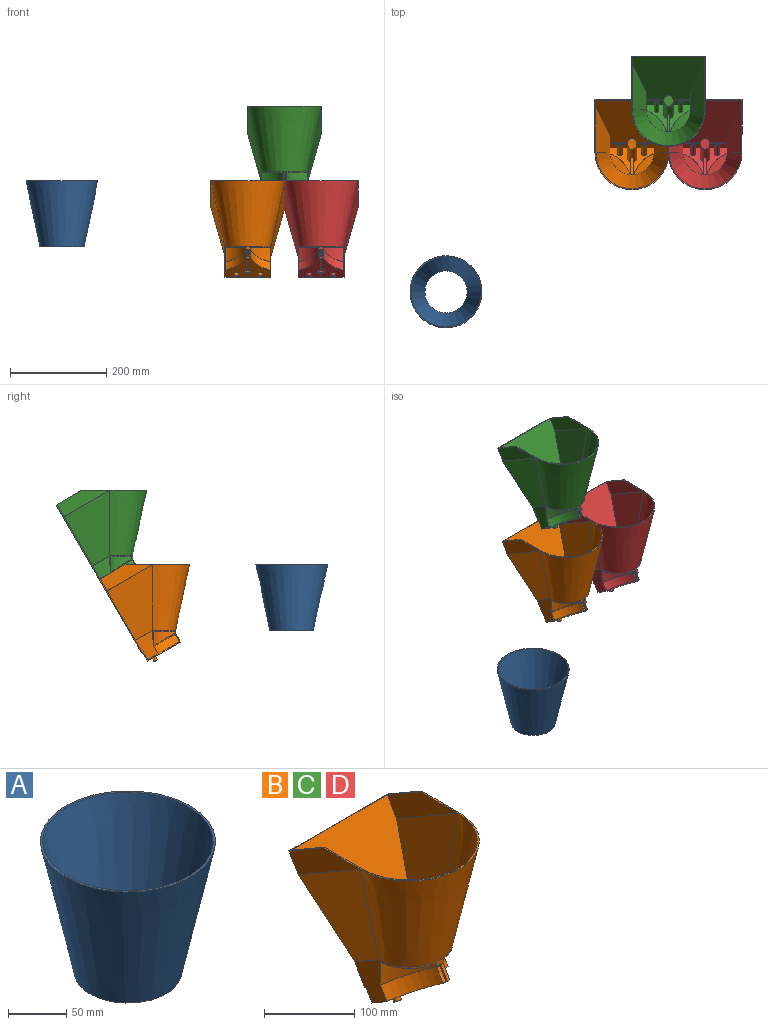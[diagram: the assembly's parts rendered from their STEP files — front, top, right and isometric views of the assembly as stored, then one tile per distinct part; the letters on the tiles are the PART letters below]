
ASSEMBLY  parts=4 mates=5
PART A: 4 faces, bbox 150x150x137 mm
  f0: cone r=73mm half-angle=12deg, axis (0,0,1), area 51428.7mm2, adj f1,f3
  f1: plane 150x150mm, normal (0,0,1), area 929.9mm2, adj f0,f2
  f2: cone r=75mm half-angle=12deg, axis (0,0,1), area 53188.7mm2, adj f1,f3
  f3: plane 91.76x91.76mm, normal (0,0,-1), area 564mm2, adj f0,f2
PART B: 80 faces, bbox 156.9x191.3x205.4 mm
  f0: plane 24.56x23.54mm, normal (-1,0,0), area 307.9mm2, adj f3,f14,f22,f74
  f1: plane 50.5x40.99mm, normal (1,0,0), area 899.7mm2, adj f2,f4,f9,f53,f74
  f2: plane 40.52x23.4mm, normal (0,-0.5,-0.87), area 93.5mm2, adj f1,f9,f10,f74
  f3: plane 68.78x46.88mm, normal (0,-0.5,-0.87), area 2119.8mm2, adj f0,f10,f14,f16,f51,f52,f74,f78
  f4: plane 68.78x46.88mm, normal (0,-0.5,-0.87), area 2119.8mm2, adj f1,f12,f17,f48,f53,f54,f74,f76
  f5: plane 37.52x21.66mm, normal (0,0.5,0.87), area 258.1mm2, adj f7,f13,f50,f66
  f6: plane 25.96x22.87mm, normal (0,0,1), area 362.8mm2, adj f50
  f7: plane 47.02x38.12mm, normal (-1,0,0), area 823.2mm2, adj f5,f50,f59,f60
  f8: cylinder r=47.88mm len=10.15mm, axis (0,0,1), area 69.5mm2, adj f9,f18,f19,f33,f45,f47,f52,f53
  f9: extruded ~2.31x2mm, area 4.6mm2, adj f1,f2,f8,f10
  f10: plane 50.5x40.99mm, normal (-1,0,0), area 899.7mm2, adj f2,f3,f9,f52,f74
  f11: plane 152.98x150mm, normal (0,-0.87,0.5), area 21352.9mm2, adj f27,f28,f29,f30,f34,f36,f49,f55
  f12: plane 24.56x23.54mm, normal (1,0,0), area 307.9mm2, adj f4,f22,f48,f74
  f13: plane 47.02x38.12mm, normal (1,0,0), area 823.2mm2, adj f5,f50,f61,f65
  f14: plane 46.88x16.45mm, normal (0,0.87,-0.5), area 890.7mm2, adj f0,f3,f16,f22
  f15: plane 154.71x154mm, normal (0,0.87,-0.5), area 22251mm2, adj f16,f17,f22,f25,f26,f35,f37,f49
  f16: plane 64.03x50.11mm, normal (1,0,0), area 1619.1mm2, adj f3,f14,f15,f19,f20,f22,f37,f39
  f17: plane 64.03x50.11mm, normal (-1,0,0), area 1619.1mm2, adj f4,f15,f18,f22,f23,f35,f38,f48
  f18: cylinder r=75mm len=45.14mm, axis (0,0,1), area 1279.3mm2, adj f8,f17,f23,f38,f46,f54
  f19: cylinder r=75mm len=45.14mm, axis (0,0,1), area 1279.3mm2, adj f8,f16,f20,f39,f44,f51
  f20: cylinder r=47.88mm len=21.65mm, axis (0,0,1), area 48.7mm2, adj f16,f19,f33,f39,f45
  f21: cylinder r=45.88mm len=5.93mm, axis (0,0,1), area 3.7mm2, adj f31,f42,f61,f67
  f22: plane 95.76x15.77mm, normal (0,-0.5,-0.87), area 223.8mm2, adj f0,f12,f14,f15,f16,f17,f48,f74
  f23: cylinder r=47.88mm len=21.65mm, axis (0,0,1), area 48.7mm2, adj f17,f18,f33,f38,f47
  f24: cylinder r=45.88mm len=5.93mm, axis (0,0,1), area 3.7mm2, adj f31,f40,f59,f67
  f25: plane 111.46x55.98mm, normal (-1,0,0), area 2518.7mm2, adj f15,f32,f35,f49
  f26: plane 111.46x55.98mm, normal (1,0,0), area 2518.7mm2, adj f15,f32,f37,f49
  f27: plane 61.4x47.08mm, normal (-1,0,0), area 1465.3mm2, adj f11,f31,f36,f42,f55,f62,f63,f65
  f28: plane 61.4x47.08mm, normal (1,0,0), area 1465.3mm2, adj f11,f31,f34,f40,f55,f57,f58,f60
  f29: plane 109.73x54.98mm, normal (1,0,0), area 2460.7mm2, adj f11,f32,f34,f49
  f30: plane 109.73x54.98mm, normal (-1,0,0), area 2460.7mm2, adj f11,f32,f36,f49
  f31: cone r=75mm half-angle=12deg, axis (0,0,1), area 26596.2mm2, adj f21,f24,f27,f28,f32,f34,f36,f40
  f32: plane 154x135mm, normal (0,0,1), area 709.5mm2, adj f25,f26,f29,f30,f31,f33,f49
  f33: cone r=77mm half-angle=12deg, axis (0,0,1), area 27474.4mm2, adj f8,f20,f23,f32,f35,f37,f45,f47
  f34: plane 157.73x95.23mm, normal (0.97,0.12,0.21), area 9249.9mm2, adj f11,f28,f29,f31
  f35: plane 158.73x96.96mm, normal (-0.97,-0.12,-0.21), area 9494.2mm2, adj f15,f17,f25,f33
  f36: plane 157.73x95.23mm, normal (-0.97,0.12,0.21), area 9249.9mm2, adj f11,f27,f30,f31
  f37: plane 158.73x96.96mm, normal (0.97,-0.12,-0.21), area 9494.2mm2, adj f15,f16,f26,f33
  f38: bspline ~9.2x4.98mm, area 2.9mm2, adj f17,f18,f23
  f39: bspline ~9.2x4.98mm, area 2.9mm2, adj f16,f19,f20
  f40: cylinder r=77mm len=44.6mm, axis (0,0,1), area 1295mm2, adj f24,f28,f31,f41,f58
  f41: plane 44.6x42.25mm, normal (0,0,1), area 761.2mm2, adj f31,f40
  f42: cylinder r=77mm len=44.6mm, axis (0,0,1), area 1295mm2, adj f21,f27,f31,f43,f62
  f43: plane 44.6x42.25mm, normal (0,0,1), area 761.2mm2, adj f31,f42
  f44: plane 45.13x42.75mm, normal (0,0,-1), area 768.8mm2, adj f19,f45
  f45: extruded ~45.11x42.74mm, area 135.3mm2, adj f8,f20,f33,f44
  f46: plane 45.13x42.75mm, normal (0,0,-1), area 768.8mm2, adj f18,f47
  f47: extruded ~45.11x42.74mm, area 135.2mm2, adj f8,f23,f33,f46
  f48: plane 46.88x16.45mm, normal (0,0.87,-0.5), area 890.7mm2, adj f4,f12,f17,f22
  f49: plane 154x53.46mm, normal (0,0.5,0.87), area 546.9mm2, adj f11,f15,f25,f26,f29,f30,f32
  f50: cylinder r=10mm len=64.67mm, axis (0,-0.5,-0.87), area 3384.3mm2, adj f5,f6,f7,f13,f55,f56,f60,f64
  f51: extruded ~55.14x43.38mm, area 1389.5mm2, adj f3,f16,f19,f52
  f52: extruded ~17.47x10.26mm, area 81.8mm2, adj f3,f8,f10,f51
  f53: extruded ~17.47x10.26mm, area 81.8mm2, adj f1,f4,f8,f54
  f54: extruded ~55.14x43.38mm, area 1389.5mm2, adj f4,f17,f18,f53
  f55: plane 91.76x13.65mm, normal (0,0.5,0.87), area 264.2mm2, adj f11,f27,f28,f50,f56,f57,f63,f64
  f56: plane 23.33x21.42mm, normal (-1,0,0), area 261.4mm2, adj f50,f55,f57,f60
  f57: plane 42.88x16.45mm, normal (0,-0.87,0.5), area 814.7mm2, adj f28,f55,f56,f60
  f58: extruded ~54.6x43.07mm, area 1369.3mm2, adj f28,f40,f59,f60
  f59: extruded ~17.35x10.04mm, area 12.4mm2, adj f7,f24,f58,f60,f66
  f60: plane 65.96x42.88mm, normal (0,0.5,0.87), area 1708.7mm2, adj f7,f28,f50,f56,f57,f58,f59,f69
  f61: extruded ~17.35x10.04mm, area 12.4mm2, adj f13,f21,f62,f65,f66
  f62: extruded ~54.6x43.07mm, area 1369.3mm2, adj f27,f42,f61,f65
  f63: plane 42.88x16.45mm, normal (0,-0.87,0.5), area 814.7mm2, adj f27,f55,f64,f65
  f64: plane 23.33x21.42mm, normal (1,0,0), area 261.4mm2, adj f50,f55,f63,f65
  f65: plane 65.96x42.88mm, normal (0,0.5,0.87), area 1708.7mm2, adj f13,f27,f50,f61,f62,f63,f64,f73
  f66: plane 6x0.87mm, normal (0,0.87,-0.5), area 6mm2, adj f5,f59,f61,f67
  f67: plane 6.02x5.91mm, normal (0,1,0), area 33.6mm2, adj f21,f24,f31,f66
  f68: cylinder r=2.5mm len=45.8mm, axis (0,-0.5,-0.87), area 785.4mm2, adj f70,f77
  f69: cylinder r=4.5mm len=39.14mm, axis (0,-0.5,-0.87), area 1131mm2, adj f60,f70
  f70: plane 9x7.79mm, normal (0,0.5,0.87), area 44mm2, adj f68,f69
  f71: plane 9x7.79mm, normal (0,0.5,0.87), area 44mm2, adj f72,f73
  f72: cylinder r=2.5mm len=45.8mm, axis (0,-0.5,-0.87), area 785.4mm2, adj f71,f79
  f73: cylinder r=4.5mm len=39.14mm, axis (0,-0.5,-0.87), area 1131mm2, adj f65,f71
  f74: cylinder r=8mm len=61.98mm, axis (0,-0.5,-0.87), area 2823.6mm2, adj f0,f1,f2,f3,f4,f10,f12,f22
  f75: plane 18.48x16mm, normal (0,0,-1), area 232.2mm2, adj f74
  f76: cylinder r=4.5mm len=11.79mm, axis (0,0.5,0.87), area 226.2mm2, adj f4,f77
  f77: plane 9x7.79mm, normal (0,-0.5,-0.87), area 44mm2, adj f68,f76
  f78: cylinder r=4.5mm len=11.79mm, axis (0,0.5,0.87), area 226.2mm2, adj f3,f79
  f79: plane 9x7.79mm, normal (0,-0.5,-0.87), area 44mm2, adj f72,f78
PART C: same geometry as B
PART D: same geometry as B
PLACE A t=(-664.17,-274.88,-44.79)mm
PLACE B t=(-277.09,14.71,-44.14)mm fixed
PLACE C t=(-201.09,104.05,110.6)mm
PLACE D t=(-125.09,14.72,-44.12)mm fixed
MATE planar D.f15 <-> B.f15  axis (0,0.87,-0.5) through (-125.09,85.97,-7.64)mm
MATE planar C.f1 <-> B.f30  axis (1,0,0) through (-202.09,71.42,82.68)mm
MATE planar B.f26 <-> D.f29  axis (1,0,0) through (-200.09,79.57,70.54)mm
MATE planar A.f0 <-> B.f31  axis (0,0,1) through (-664.17,-274.88,23.71)mm
MATE planar C.f48 <-> B.f11  axis (0,0.87,-0.5) through (-225.53,119.71,54.79)mm
